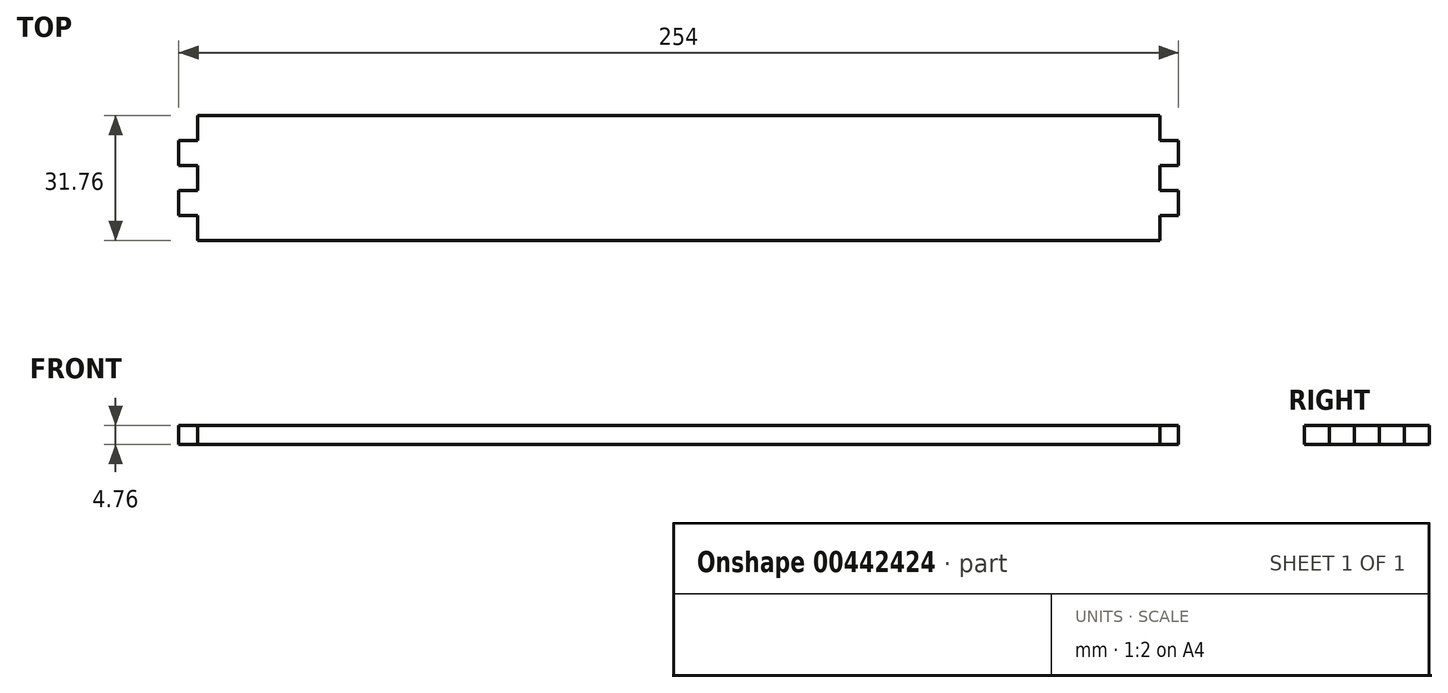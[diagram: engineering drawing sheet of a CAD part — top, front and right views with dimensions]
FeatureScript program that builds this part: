
annotation { "Feature Type Name" : "Feature", "Feature Type Description" : "" }
export const myFeature = defineFeature(function(context is Context, id is Id, definition is map)
    precondition{}
    {
        {
            var Q0;
            Q0=qCreatedBy(makeId("Top.planeOp"),FACE);
            var sketch = newSketch(context, id + "F0", { "sketchPlane" : qUnion([Q0])});
            skLineSegment(sketch, "E0.bottom", {"start": v(-122.24, 15.87) * mm, "end": v(122.24, 15.87) * mm});
            skLineSegment(sketch, "E0.top", {"start": v(-122.24, -15.87) * mm, "end": v(122.24, -15.87) * mm});
            skPoint(sketch, "E0.middle", {"position": v(0, 0) * mm});
            skLineSegment(sketch, "E1", {"start": v(-127, 9.53) * mm, "end": v(-122.24, 9.53) * mm});
            skLineSegment(sketch, "E2", {"start": v(-122.24, 3.17) * mm, "end": v(-127, 3.17) * mm});
            skLineSegment(sketch, "E3", {"start": v(0, 0) * mm, "end": v(0, 15.87) * mm, "construction": true});
            skLineSegment(sketch, "E4.0.1.0", {"start": v(-127, -3.18) * mm, "end": v(-122.24, -3.18) * mm});
            skLineSegment(sketch, "E4.0.1.1", {"start": v(-122.24, -9.53) * mm, "end": v(-127, -9.53) * mm});
            skLineSegment(sketch, "E4.direction1", {"start": v(-127, 9.53) * mm, "end": v(-101.6, 9.53) * mm, "construction": true});
            skLineSegment(sketch, "E5.MirrorCS", {"start": v(122.24, 3.17) * mm, "end": v(127, 3.17) * mm});
            skLineSegment(sketch, "E6.MirrorCS", {"start": v(127, -3.18) * mm, "end": v(122.24, -3.18) * mm});
            skLineSegment(sketch, "E7.MirrorCS", {"start": v(122.24, -9.53) * mm, "end": v(127, -9.53) * mm});
            skLineSegment(sketch, "E8", {"start": v(122.24, 9.52) * mm, "end": v(127, 9.52) * mm});
            skLineSegment(sketch, "E9", {"start": v(-127, 9.53) * mm, "end": v(-127, 3.17) * mm});
            skLineSegment(sketch, "E10", {"start": v(-127, -3.18) * mm, "end": v(-127, -9.53) * mm});
            skLineSegment(sketch, "E11", {"start": v(-122.24, -9.53) * mm, "end": v(-122.24, -15.87) * mm});
            skLineSegment(sketch, "E12", {"start": v(-122.24, 9.53) * mm, "end": v(-122.24, 15.87) * mm});
            skPoint(sketch, "E13.orphan", {"position": v(-127, 15.87) * mm});
            skLineSegment(sketch, "E14", {"start": v(-122.24, 3.17) * mm, "end": v(-122.24, -3.18) * mm});
            skPoint(sketch, "E15.orphan", {"position": v(-127, -15.87) * mm});
            skLineSegment(sketch, "E16", {"start": v(127, 3.17) * mm, "end": v(127, 9.52) * mm});
            skLineSegment(sketch, "E17", {"start": v(127, -3.18) * mm, "end": v(127, -9.53) * mm});
            skLineSegment(sketch, "E18", {"start": v(122.24, -9.53) * mm, "end": v(122.24, -15.87) * mm});
            skLineSegment(sketch, "E19", {"start": v(122.24, -15.87) * mm, "end": v(122.24, -9.53) * mm});
            skLineSegment(sketch, "E20", {"start": v(122.24, 3.17) * mm, "end": v(122.24, -3.18) * mm});
            skLineSegment(sketch, "E21", {"start": v(122.24, 9.52) * mm, "end": v(122.24, 15.87) * mm});
            skPoint(sketch, "E0.right.start.orphan", {"position": v(127, 15.87) * mm});
            skPoint(sketch, "E22.trimOffspring.end.orphan", {"position": v(127, -15.87) * mm});
            skSolve(sketch);
        }
        {
            var Q0;
            Q0 = qSketchRegion(id + "F0", true);
            extrude(context, id + "F1", {"entities" : qUnion([Q0]), "depth" : 4.76 * mm});
        }
    });
